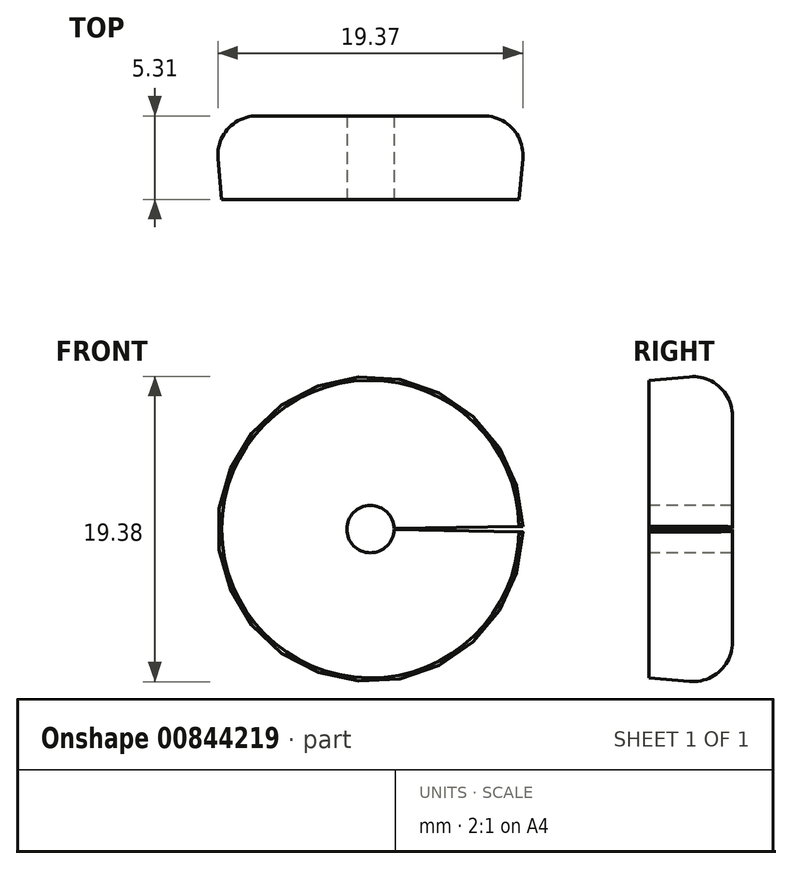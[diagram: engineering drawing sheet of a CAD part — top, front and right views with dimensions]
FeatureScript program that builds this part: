
annotation { "Feature Type Name" : "Feature", "Feature Type Description" : "" }
export const myFeature = defineFeature(function(context is Context, id is Id, definition is map)
    precondition{}
    {
        {
            var Q0;
            Q0=qCreatedBy(makeId("Top.planeOp"),FACE);
            var sketch = newSketch(context, id + "F0", { "sketchPlane" : qUnion([Q0])});
            skLineSegment(sketch, "E0", {"start": v(0, 0) * mm, "end": v(0, 8.7) * mm, "construction": true});
            skLineSegment(sketch, "E1", {"start": v(1.5, 0) * mm, "end": v(1.5, 5.3) * mm});
            skLineSegment(sketch, "E2", {"start": v(9.45, 0) * mm, "end": v(9.68, 2.59) * mm});
            skLineSegment(sketch, "E3", {"start": v(9.45, 0) * mm, "end": v(1.5, 0) * mm});
            skLineSegment(sketch, "E4", {"start": v(7.19, 5.3) * mm, "end": v(1.5, 5.3) * mm});
            skPoint(sketch, "E5.visualSharp", {"position": v(9.91, 5.3) * mm});
            skArc(sketch, "E5.filletArc", {"start": v(9.68, 2.59) * mm, "mid": v(9.03, 4.5) * mm, "end": v(7.19, 5.3) * mm});
            skSolve(sketch);
        }
        {
            var Q0;
            Q0=makeQuery(id+"F0.imprint","IMPRINT",FACE,{"disambiguationData":[TD([[makeQuery(id+"F0.imprint","IMPRINT",EDGE,{"derivedFrom":sQuery(id+"F0.wireOp",EDGE,"E1")}),-1.0]])]});
            var Q1;
            Q1=sQuery(id+"F0.wireOp",EDGE,"E0");
            revolve(context, id + "F1", {"surfaceOperationType" : NewSurfaceOperationType.NEW, "entities" : qUnion([Q0]), "axis" : qUnion([Q1]), "revolveType" : RevolveType.FULL});
        }
        {
            var Q0;
            Q0=makeQuery(id+"F1.opRevolve","SWEPT_FACE",FACE,{"disambiguationData":[OSD([sQuery(id+"F0.wireOp",EDGE,"E3")])]});
            var sketch = newSketch(context, id + "F2", { "sketchPlane" : qUnion([Q0])});
            skLineSegment(sketch, "E6", {"start": v(0, 0) * mm, "end": v(11.26, -0.2) * mm});
            skLineSegment(sketch, "E7", {"start": v(11.26, -0.2) * mm, "end": v(11.26, 0) * mm});
            skLineSegment(sketch, "E8.MirrorCS", {"start": v(0, 0) * mm, "end": v(11.26, 0.2) * mm});
            skLineSegment(sketch, "E9.MirrorCS", {"start": v(11.26, 0.2) * mm, "end": v(11.26, 0) * mm});
            skSolve(sketch);
        }
        {
            var Q0;
            {var subQ4=sQuery(id+"F2.wireOp",EDGE,"E7");Q0=makeQuery(id+"F2.imprint","IMPRINT",FACE,{"disambiguationData":[TD([[makeQuery(id+"F2.imprint","IMPRINT",EDGE,{"derivedFrom":subQ4}),1.0]])]});}
            var Q1;
            {var subQ0=sQuery(id+"F2.wireOp",EDGE,"E6");var subQ1=sQuery(id+"F0.wireOp",EDGE,"E3");var subQ2=makeQuery(id+"F1.opRevolve","SWEPT_EDGE",EDGE,{"disambiguationData":[OSD([sQuery(id+"F0.wireOp",EDGE,"E2"),subQ1])]});var subQ3=makeQuery(id+"F2.imprint","INTERSECT",VERTEX,{"derivedFrom":[subQ2,subQ0]});Q1=makeQuery(id+"F2.imprint","IMPRINT",FACE,{"disambiguationData":[TD([[makeQuery(id+"F2.imprint","IMPRINT",EDGE,{"disambiguationData":[TD([[subQ3,1.0]])],"derivedFrom":subQ0}),1.0]])]});}
            extrude(context, id + "F3", {"entities" : qUnion([Q0, Q1]), "operationType" : NewBodyOperationType.REMOVE, "oppositeDirection" : true, "depth" : 25 * mm, "offsetDistance" : 25 * mm});
        }
    });
